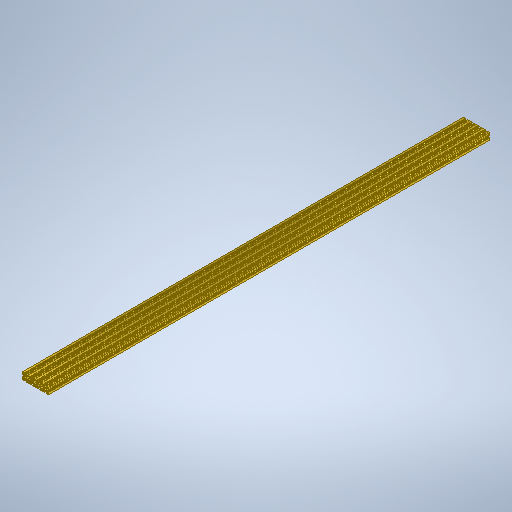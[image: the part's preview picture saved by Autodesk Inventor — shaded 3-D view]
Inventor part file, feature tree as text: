
AUTODESK INVENTOR PART (.ipt)
format: ipt  version: 2025.2 (Build 292293000, 293)  size: 658,944 bytes
history: native  units: mm
features: mirror x2, other x1, extrude x1, sketch x1
ambient origin geometry x8: Origin, YZ Plane, XZ Plane, XY Plane, X Axis, Y Axis, Z Axis, Center Point
bodies: Body1 (feature_tree)
feature tree (5):
  other  "Sólido1"
  extrude  "Extrusão1"  Depth=15.0mm
  mirror  "Espelhar1"
  mirror  "Espelhar2"
  sketch  "Esboço2"  dims[d45=10.0mm d46=15.0mm d48=15.0mm d49=15.0mm d50=8.2mm d51=8.0mm d55=2.2mm d61=1.1mm d62=1.1mm d64=30.0mm d75=2.2mm d81=4.5mm d83=1.1mm d86=2000.0mm d87=0.0mm]
